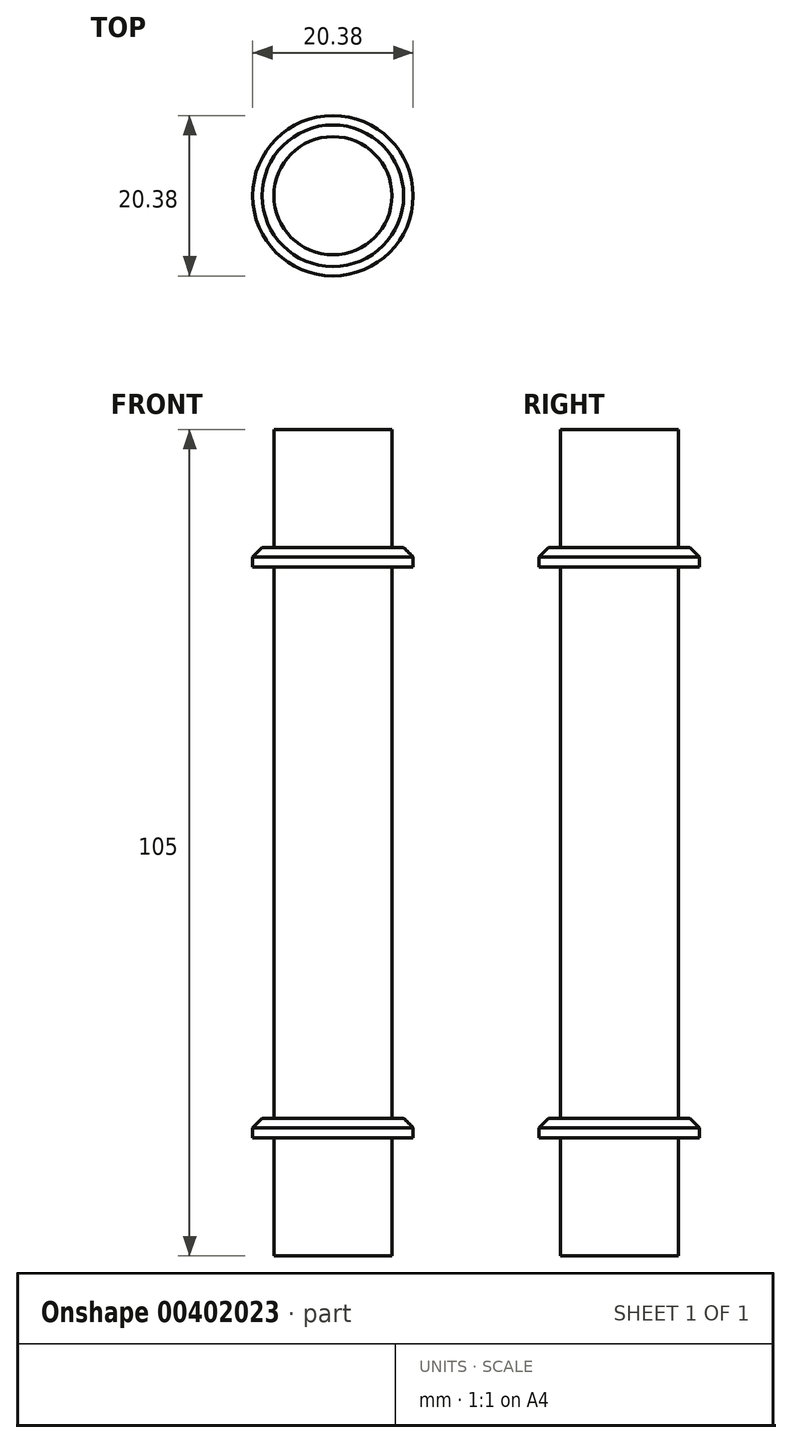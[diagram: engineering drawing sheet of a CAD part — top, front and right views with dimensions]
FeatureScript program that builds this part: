
annotation { "Feature Type Name" : "Feature", "Feature Type Description" : "" }
export const myFeature = defineFeature(function(context is Context, id is Id, definition is map)
    precondition{}
    {
        {
            var Q0;
            Q0=qCreatedBy(makeId("Front.planeOp"),FACE);
            var sketch = newSketch(context, id + "F0", { "sketchPlane" : qUnion([Q0])});
            skLineSegment(sketch, "E0", {"start": v(0, 95.6) * mm, "end": v(0, -95.28) * mm, "construction": true});
            skLineSegment(sketch, "E1", {"start": v(0, 52.5) * mm, "end": v(7.5, 52.5) * mm});
            skLineSegment(sketch, "E2", {"start": v(7.5, 52.5) * mm, "end": v(7.5, 37.5) * mm});
            skLineSegment(sketch, "E3", {"start": v(7.5, -52.5) * mm, "end": v(0, -52.5) * mm});
            skLineSegment(sketch, "E4", {"start": v(7.5, 37.5) * mm, "end": v(10.2, 37.5) * mm});
            skLineSegment(sketch, "E5", {"start": v(10.2, 37.5) * mm, "end": v(10.2, 35) * mm});
            skLineSegment(sketch, "E6", {"start": v(10.2, 35) * mm, "end": v(7.5, 35) * mm});
            skLineSegment(sketch, "E7", {"start": v(7.5, -35) * mm, "end": v(10.2, -35) * mm});
            skLineSegment(sketch, "E8", {"start": v(10.2, -35) * mm, "end": v(10.2, -37.5) * mm});
            skLineSegment(sketch, "E9", {"start": v(10.2, -37.5) * mm, "end": v(7.5, -37.5) * mm});
            skLineSegment(sketch, "E10.trimOffspring", {"start": v(7.5, 35) * mm, "end": v(7.5, -35) * mm});
            skLineSegment(sketch, "E11.trimOffspring", {"start": v(7.5, -37.5) * mm, "end": v(7.5, -52.5) * mm});
            skLineSegment(sketch, "E12", {"start": v(0, 52.5) * mm, "end": v(0, -52.5) * mm});
            skSolve(sketch);
        }
        {
            var Q0;
            Q0=makeQuery(id+"F0.imprint","IMPRINT",FACE,{"disambiguationData":[TD([[makeQuery(id+"F0.imprint","IMPRINT",EDGE,{"derivedFrom":sQuery(id+"F0.wireOp",EDGE,"E1")}),-1.0]])]});
            var Q1;
            Q1=sQuery(id+"F0.wireOp",EDGE,"E0");
            revolve(context, id + "F1", {"entities" : qUnion([Q0]), "axis" : qUnion([Q1]), "revolveType" : RevolveType.FULL});
        }
        {
            var Q0;
            Q0=makeQuery(id+"F1.opRevolve","SWEPT_EDGE",EDGE,{"disambiguationData":[OSD([sQuery(id+"F0.wireOp",EDGE,"E4"),sQuery(id+"F0.wireOp",EDGE,"E5")])]});
            var Q1;
            Q1=makeQuery(id+"F1.opRevolve","SWEPT_EDGE",EDGE,{"disambiguationData":[OSD([sQuery(id+"F0.wireOp",EDGE,"E7"),sQuery(id+"F0.wireOp",EDGE,"E8")])]});
            chamfer(context, id + "F2", {"entities" : qUnion([Q0, Q1]), "width" : 1.2 * mm, "tangentPropagation" : true});
        }
    });
